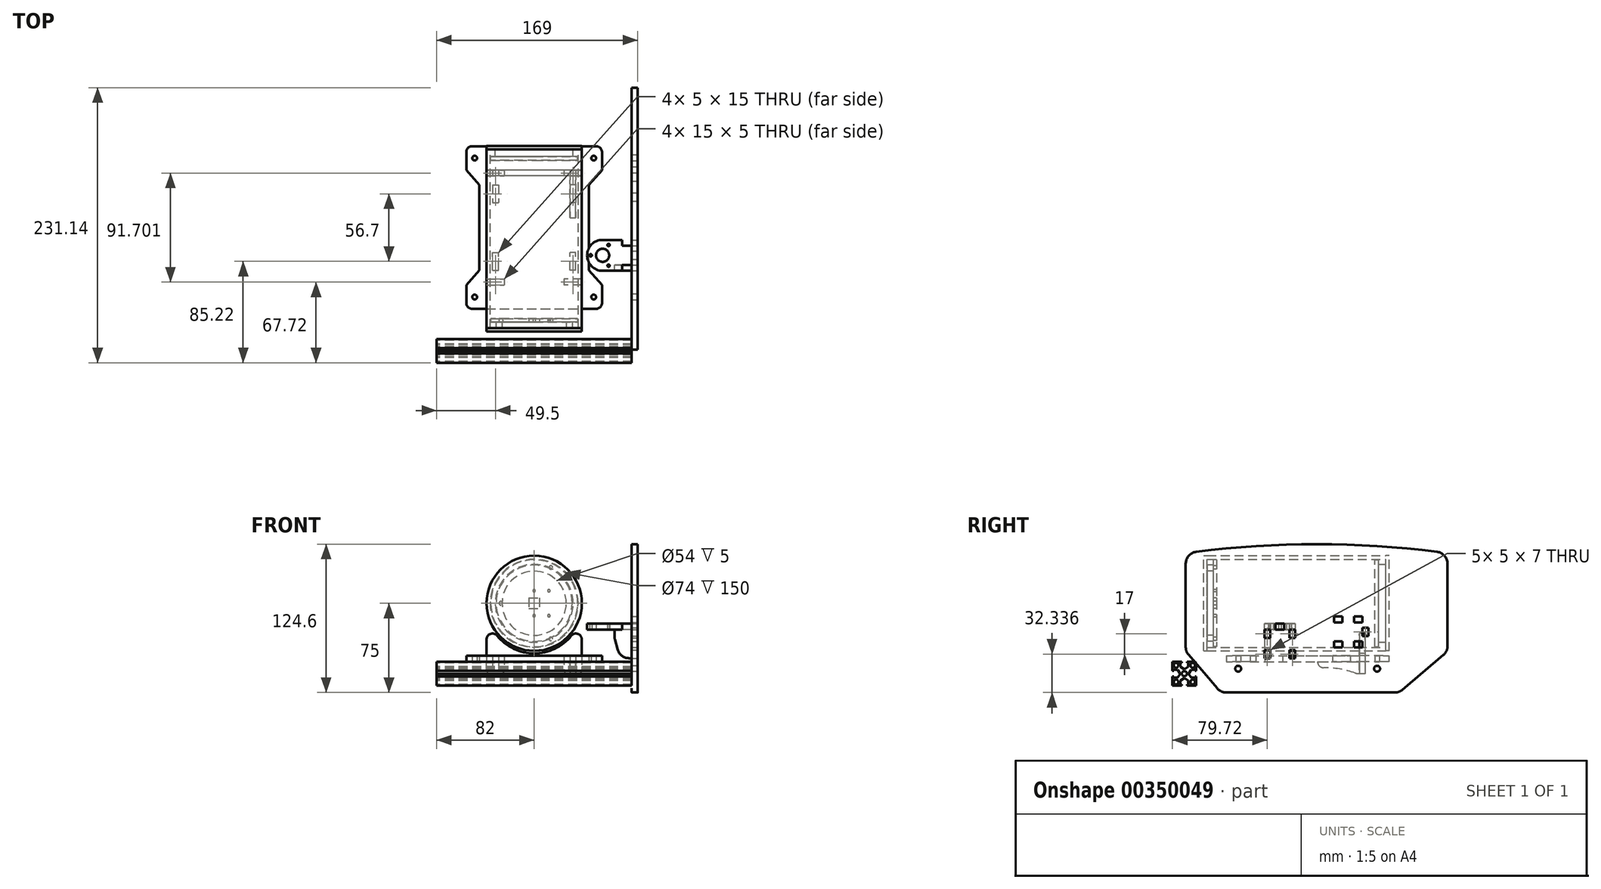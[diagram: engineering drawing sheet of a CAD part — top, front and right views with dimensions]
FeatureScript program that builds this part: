
annotation { "Feature Type Name" : "Feature", "Feature Type Description" : "" }
export const myFeature = defineFeature(function(context is Context, id is Id, definition is map)
    precondition{}
    {
        {
            var Q0;
            Q0=qCreatedBy(makeId("Front.planeOp"),FACE);
            var sketch = newSketch(context, id + "F0", { "sketchPlane" : qUnion([Q0])});
            skCircle(sketch, "E0", {"center": v(0, 0) * mm, "radius": 40 * mm});
            skCircle(sketch, "E1.0", {"center": v(0, 0) * mm, "radius": 37 * mm});
            skSolve(sketch);
        }
        {
            var Q0;
            Q0 = qSketchRegion(id + "F0", true);
            extrude(context, id + "F1", {"entities" : qUnion([Q0]), "depth" : 150 * mm});
        }
        {
            var Q0;
            Q0=makeQuery(id+"F1.opExtrude","CAP_FACE",FACE,{"disambiguationData":[OSD([sQuery(id+"F0.wireOp",EDGE,"E0"),sQuery(id+"F0.wireOp",EDGE,"E1.0")])],"isStart":false});
            var sketch = newSketch(context, id + "F2", { "sketchPlane" : qUnion([Q0])});
            skCircle(sketch, "E2", {"center": v(0, 0) * mm, "radius": 40 * mm});
            skSolve(sketch);
        }
        {
            var Q0;
            Q0=qSketchRegion(id+"F2",true);
            extrude(context, id + "F3", {"entities" : qUnion([Q0]), "depth" : 3 * mm});
        }
        {
            var Q0;
            Q0=makeQuery(id+"F3.opExtrude","CAP_FACE",FACE,{"disambiguationData":[OSD([sQuery(id+"F2.wireOp",EDGE,"E2")])],"isStart":true});
            var sketch = newSketch(context, id + "F4", { "sketchPlane" : qUnion([Q0])});
            skCircle(sketch, "E3", {"center": v(0, 0) * mm, "radius": 32 * mm});
            skCircle(sketch, "E4", {"center": v(0, 0) * mm, "radius": 27 * mm});
            skSolve(sketch);
        }
        {
            var Q0;
            Q0=qSketchRegion(id+"F4",true);
            extrude(context, id + "F5", {"entities" : qUnion([Q0]), "depth" : 5 * mm});
        }
        {
            var Q0;
            Q0=makeQuery(id+"F1.opExtrude","CAP_FACE",FACE,{"disambiguationData":[OSD([sQuery(id+"F0.wireOp",EDGE,"E0"),sQuery(id+"F0.wireOp",EDGE,"E1.0")])],"isStart":true});
            var sketch = newSketch(context, id + "F6", { "sketchPlane" : qUnion([Q0])});
            skCircle(sketch, "E5", {"center": v(0, 0) * mm, "radius": 40 * mm});
            skSolve(sketch);
        }
        {
            var Q0;
            Q0=qSketchRegion(id+"F6",true);
            extrude(context, id + "F7", {"entities" : qUnion([Q0]), "depth" : 3 * mm});
        }
        {
            var Q0;
            Q0=makeQuery(id+"F7.opExtrude","CAP_FACE",FACE,{"disambiguationData":[OSD([sQuery(id+"F6.wireOp",EDGE,"E5")])],"isStart":true});
            var sketch = newSketch(context, id + "F8", { "sketchPlane" : qUnion([Q0])});
            skCircle(sketch, "E6", {"center": v(0, 0) * mm, "radius": 37 * mm, "construction": true});
            skCircle(sketch, "E7", {"center": v(0, 0) * mm, "radius": 32.7 * mm});
            skSolve(sketch);
        }
        {
            var Q0;
            Q0=qSketchRegion(id+"F8",true);
            extrude(context, id + "F9", {"entities" : qUnion([Q0]), "depth" : 6 * mm});
        }
        {
            var Q0;
            Q0=makeQuery(id+"F9.opExtrude","CAP_FACE",FACE,{"disambiguationData":[OSD([sQuery(id+"F8.wireOp",EDGE,"E7")])],"isStart":false});
            var sketch = newSketch(context, id + "F10", { "sketchPlane" : qUnion([Q0])});
            skCircle(sketch, "E8", {"center": v(0, 0) * mm, "radius": 36.5 * mm});
            skSolve(sketch);
        }
        {
            var Q0;
            Q0=qSketchRegion(id+"F10",true);
            extrude(context, id + "F11", {"entities" : qUnion([Q0]), "depth" : 3 * mm});
        }
        {
            var Q0;
            Q0=makeQuery(id+"F5.opExtrude","CAP_FACE",FACE,{"disambiguationData":[OSD([sQuery(id+"F4.wireOp",EDGE,"E3"),sQuery(id+"F4.wireOp",EDGE,"E4")])],"isStart":false});
            var sketch = newSketch(context, id + "F12", { "sketchPlane" : qUnion([Q0])});
            skCircle(sketch, "E9", {"center": v(0, 0) * mm, "radius": 36.5 * mm});
            skCircle(sketch, "E10", {"center": v(28, 0) * mm, "radius": 1.5 * mm});
            skCircle(sketch, "E11", {"center": v(-14, 30) * mm, "radius": 1.5 * mm});
            skLineSegment(sketch, "E12", {"start": v(0, 0) * mm, "end": v(11.11, 0) * mm, "construction": true});
            skCircle(sketch, "E13.MirrorC", {"center": v(-14, -30) * mm, "radius": 1.5 * mm});
            skLineSegment(sketch, "E14.bottom", {"start": v(4.5, 4.5) * mm, "end": v(-4.5, 4.5) * mm});
            skLineSegment(sketch, "E14.top", {"start": v(4.5, -4.5) * mm, "end": v(-4.5, -4.5) * mm});
            skLineSegment(sketch, "E14.left", {"start": v(4.5, 4.5) * mm, "end": v(4.5, -4.5) * mm});
            skLineSegment(sketch, "E14.right", {"start": v(-4.5, 4.5) * mm, "end": v(-4.5, -4.5) * mm});
            skLineSegment(sketch, "E15.bottom", {"start": v(9.6, 12.5) * mm, "end": v(-14.4, 12.5) * mm, "construction": true});
            skLineSegment(sketch, "E15.top", {"start": v(9.6, -12.5) * mm, "end": v(-14.4, -12.5) * mm, "construction": true});
            skLineSegment(sketch, "E15.left", {"start": v(9.6, 12.5) * mm, "end": v(9.6, -12.5) * mm, "construction": true});
            skLineSegment(sketch, "E15.right", {"start": v(-14.4, 12.5) * mm, "end": v(-14.4, -12.5) * mm, "construction": true});
            skPoint(sketch, "E15.middle", {"position": v(-2.4, 0) * mm});
            skCircle(sketch, "E16", {"center": v(0.1, 10.5) * mm, "radius": 1.05 * mm});
            skCircle(sketch, "E17", {"center": v(-12.4, 10.5) * mm, "radius": 1.05 * mm});
            skCircle(sketch, "E18", {"center": v(-12.4, -10.5) * mm, "radius": 1.05 * mm});
            skCircle(sketch, "E19", {"center": v(0.1, -10.5) * mm, "radius": 1.05 * mm});
            skSolve(sketch);
        }
        {
            var Q0;
            Q0=qSketchRegion(id+"F12",true);
            extrude(context, id + "F13", {"entities" : qUnion([Q0]), "depth" : 3 * mm});
        }
        {
            var Q0;
            Q0=qCreatedBy(makeId("Right.planeOp"),FACE);
            var sketch = newSketch(context, id + "F14", { "sketchPlane" : qUnion([Q0])});
            skLineSegment(sketch, "E20.bottom", {"start": v(-159.14, -49.16) * mm, "end": v(-179.14, -49.16) * mm});
            skLineSegment(sketch, "E20.top", {"start": v(-159.14, -69.16) * mm, "end": v(-179.14, -69.16) * mm});
            skLineSegment(sketch, "E20.left", {"start": v(-159.14, -49.16) * mm, "end": v(-159.14, -69.16) * mm});
            skLineSegment(sketch, "E20.right", {"start": v(-179.14, -49.16) * mm, "end": v(-179.14, -69.16) * mm});
            skPoint(sketch, "E20.middle", {"position": v(-169.14, -59.16) * mm});
            skCircle(sketch, "E21", {"center": v(-169.14, -59.16) * mm, "radius": 2.15 * mm});
            skLineSegment(sketch, "E22", {"start": v(-169.14, -49.16) * mm, "end": v(-169.14, -69.16) * mm, "construction": true});
            skLineSegment(sketch, "E23", {"start": v(-179.14, -59.16) * mm, "end": v(-159.14, -59.16) * mm, "construction": true});
            skCircle(sketch, "E24", {"center": v(-176.14, -52.16) * mm, "radius": 2 * mm});
            skLineSegment(sketch, "E25", {"start": v(-169.14, -59.16) * mm, "end": v(-179.14, -49.16) * mm, "construction": true});
            skLineSegment(sketch, "E26", {"start": v(-171.44, -49.16) * mm, "end": v(-171.44, -50.16) * mm});
            skLineSegment(sketch, "E27", {"start": v(-171.44, -50.16) * mm, "end": v(-172.44, -50.16) * mm});
            skLineSegment(sketch, "E28", {"start": v(-172.44, -50.16) * mm, "end": v(-172.44, -53.36) * mm});
            skLineSegment(sketch, "E29", {"start": v(-172.44, -53.36) * mm, "end": v(-169.14, -55.66) * mm});
            skLineSegment(sketch, "E30.MirrorCS", {"start": v(-174.94, -55.86) * mm, "end": v(-172.64, -59.16) * mm});
            skLineSegment(sketch, "E31.MirrorCS", {"start": v(-178.14, -55.86) * mm, "end": v(-174.94, -55.86) * mm});
            skLineSegment(sketch, "E32.MirrorCS", {"start": v(-178.14, -56.86) * mm, "end": v(-178.14, -55.86) * mm});
            skLineSegment(sketch, "E33.MirrorCS", {"start": v(-179.14, -56.86) * mm, "end": v(-178.14, -56.86) * mm});
            skLineSegment(sketch, "E34.MirrorCS", {"start": v(-166.84, -49.16) * mm, "end": v(-166.84, -50.16) * mm});
            skLineSegment(sketch, "E35.MirrorCS", {"start": v(-166.84, -50.16) * mm, "end": v(-165.84, -50.16) * mm});
            skLineSegment(sketch, "E36.MirrorCS", {"start": v(-165.84, -50.16) * mm, "end": v(-165.84, -53.36) * mm});
            skLineSegment(sketch, "E37.MirrorCS", {"start": v(-165.84, -53.36) * mm, "end": v(-169.14, -55.66) * mm});
            skLineSegment(sketch, "E38.MirrorCS", {"start": v(-163.34, -55.86) * mm, "end": v(-165.64, -59.16) * mm});
            skLineSegment(sketch, "E39.MirrorCS", {"start": v(-160.14, -55.86) * mm, "end": v(-163.34, -55.86) * mm});
            skLineSegment(sketch, "E40.MirrorCS", {"start": v(-160.14, -56.86) * mm, "end": v(-160.14, -55.86) * mm});
            skLineSegment(sketch, "E41.MirrorCS", {"start": v(-159.14, -56.86) * mm, "end": v(-160.14, -56.86) * mm});
            skCircle(sketch, "E42.MirrorC", {"center": v(-162.14, -52.16) * mm, "radius": 2 * mm});
            skLineSegment(sketch, "E43.MirrorCS", {"start": v(-174.94, -62.46) * mm, "end": v(-172.64, -59.16) * mm});
            skLineSegment(sketch, "E44.MirrorCS", {"start": v(-178.14, -62.46) * mm, "end": v(-174.94, -62.46) * mm});
            skLineSegment(sketch, "E45.MirrorCS", {"start": v(-178.14, -61.46) * mm, "end": v(-178.14, -62.46) * mm});
            skLineSegment(sketch, "E46.MirrorCS", {"start": v(-179.14, -61.46) * mm, "end": v(-178.14, -61.46) * mm});
            skLineSegment(sketch, "E47.MirrorCS", {"start": v(-163.34, -62.46) * mm, "end": v(-165.64, -59.16) * mm});
            skLineSegment(sketch, "E48.MirrorCS", {"start": v(-160.14, -62.46) * mm, "end": v(-163.34, -62.46) * mm});
            skLineSegment(sketch, "E49.MirrorCS", {"start": v(-160.14, -61.46) * mm, "end": v(-160.14, -62.46) * mm});
            skLineSegment(sketch, "E50.MirrorCS", {"start": v(-159.14, -61.46) * mm, "end": v(-160.14, -61.46) * mm});
            skCircle(sketch, "E51.MirrorC", {"center": v(-162.14, -66.16) * mm, "radius": 2 * mm});
            skCircle(sketch, "E52.MirrorC", {"center": v(-176.14, -66.16) * mm, "radius": 2 * mm});
            skLineSegment(sketch, "E53.MirrorCS", {"start": v(-172.44, -64.96) * mm, "end": v(-169.14, -62.66) * mm});
            skLineSegment(sketch, "E54.MirrorCS", {"start": v(-172.44, -68.16) * mm, "end": v(-172.44, -64.96) * mm});
            skLineSegment(sketch, "E55.MirrorCS", {"start": v(-171.44, -68.16) * mm, "end": v(-172.44, -68.16) * mm});
            skLineSegment(sketch, "E56.MirrorCS", {"start": v(-171.44, -69.16) * mm, "end": v(-171.44, -68.16) * mm});
            skLineSegment(sketch, "E57.MirrorCS", {"start": v(-166.84, -69.16) * mm, "end": v(-166.84, -68.16) * mm});
            skLineSegment(sketch, "E58.MirrorCS", {"start": v(-166.84, -68.16) * mm, "end": v(-165.84, -68.16) * mm});
            skLineSegment(sketch, "E59.MirrorCS", {"start": v(-165.84, -68.16) * mm, "end": v(-165.84, -64.96) * mm});
            skLineSegment(sketch, "E60.MirrorCS", {"start": v(-165.84, -64.96) * mm, "end": v(-169.14, -62.66) * mm});
            skSolve(sketch);
        }
        {
            var Q0;
            Q0=makeQuery(id+"F14.imprint","IMPRINT",FACE,{"disambiguationData":[TD([[makeQuery(id+"F14.imprint","IMPRINT",EDGE,{"derivedFrom":sQuery(id+"F14.wireOp",EDGE,"E21")}),-1.0]])]});
            extrude(context, id + "F15", {"entities" : qUnion([Q0]), "depth" : 82 * mm, "hasSecondDirection" : true, "secondDirectionOppositeDirection" : true, "secondDirectionDepth" : 82 * mm});
        }
        {
            var Q0;
            Q0=makeQuery(id+"F15.opExtrude","CAP_FACE",FACE,{"disambiguationData":[OSD([sQuery(id+"F14.wireOp",EDGE,"E20.bottom"),sQuery(id+"F14.wireOp",EDGE,"E20.top"),sQuery(id+"F14.wireOp",EDGE,"E20.left"),sQuery(id+"F14.wireOp",EDGE,"E20.right"),sQuery(id+"F14.wireOp",EDGE,"E21"),sQuery(id+"F14.wireOp",EDGE,"E24"),sQuery(id+"F14.wireOp",EDGE,"E26"),sQuery(id+"F14.wireOp",EDGE,"E27"),sQuery(id+"F14.wireOp",EDGE,"E28"),sQuery(id+"F14.wireOp",EDGE,"E29"),sQuery(id+"F14.wireOp",EDGE,"E30.MirrorCS"),sQuery(id+"F14.wireOp",EDGE,"E31.MirrorCS"),sQuery(id+"F14.wireOp",EDGE,"E32.MirrorCS"),sQuery(id+"F14.wireOp",EDGE,"E33.MirrorCS"),sQuery(id+"F14.wireOp",EDGE,"E34.MirrorCS"),sQuery(id+"F14.wireOp",EDGE,"E35.MirrorCS"),sQuery(id+"F14.wireOp",EDGE,"E36.MirrorCS"),sQuery(id+"F14.wireOp",EDGE,"E37.MirrorCS"),sQuery(id+"F14.wireOp",EDGE,"E38.MirrorCS"),sQuery(id+"F14.wireOp",EDGE,"E39.MirrorCS"),sQuery(id+"F14.wireOp",EDGE,"E40.MirrorCS"),sQuery(id+"F14.wireOp",EDGE,"E41.MirrorCS"),sQuery(id+"F14.wireOp",EDGE,"E42.MirrorC"),sQuery(id+"F14.wireOp",EDGE,"E43.MirrorCS"),sQuery(id+"F14.wireOp",EDGE,"E44.MirrorCS"),sQuery(id+"F14.wireOp",EDGE,"E45.MirrorCS"),sQuery(id+"F14.wireOp",EDGE,"E46.MirrorCS"),sQuery(id+"F14.wireOp",EDGE,"E47.MirrorCS"),sQuery(id+"F14.wireOp",EDGE,"E48.MirrorCS"),sQuery(id+"F14.wireOp",EDGE,"E49.MirrorCS"),sQuery(id+"F14.wireOp",EDGE,"E50.MirrorCS"),sQuery(id+"F14.wireOp",EDGE,"E51.MirrorC"),sQuery(id+"F14.wireOp",EDGE,"E52.MirrorC"),sQuery(id+"F14.wireOp",EDGE,"E53.MirrorCS"),sQuery(id+"F14.wireOp",EDGE,"E54.MirrorCS"),sQuery(id+"F14.wireOp",EDGE,"E55.MirrorCS"),sQuery(id+"F14.wireOp",EDGE,"E56.MirrorCS"),sQuery(id+"F14.wireOp",EDGE,"E57.MirrorCS"),sQuery(id+"F14.wireOp",EDGE,"E58.MirrorCS"),sQuery(id+"F14.wireOp",EDGE,"E59.MirrorCS"),sQuery(id+"F14.wireOp",EDGE,"E60.MirrorCS")])],"isStart":false});
            var sketch = newSketch(context, id + "F16", { "sketchPlane" : qUnion([Q0])});
            skLineSegment(sketch, "E61", {"start": v(-141.53, -71.49) * mm, "end": v(-165.6, -43.24) * mm});
            skLineSegment(sketch, "E62", {"start": v(-168, -36.76) * mm, "end": v(-168, 33.24) * mm});
            skLineSegment(sketch, "E63", {"start": v(-133.92, -75) * mm, "end": v(7.78, -75) * mm});
            skLineSegment(sketch, "E64", {"start": v(14.27, -72.6) * mm, "end": v(48.49, -43.43) * mm});
            skLineSegment(sketch, "E65", {"start": v(52, -35.83) * mm, "end": v(52, 33.24) * mm});
            skArc(sketch, "E66", {"start": v(43.27, 43.16) * mm, "mid": v(-58, 49.6) * mm, "end": v(-159.27, 43.16) * mm});
            skPoint(sketch, "E67.visualSharp", {"position": v(-168, 42) * mm});
            skArc(sketch, "E67.filletArc", {"start": v(-159.27, 43.16) * mm, "mid": v(-165.5, 39.85) * mm, "end": v(-168, 33.24) * mm});
            skPoint(sketch, "E68.visualSharp", {"position": v(52, 42) * mm});
            skArc(sketch, "E68.filletArc", {"start": v(52, 33.24) * mm, "mid": v(49.5, 39.85) * mm, "end": v(43.27, 43.16) * mm});
            skPoint(sketch, "E69.visualSharp", {"position": v(-168, -40.44) * mm});
            skArc(sketch, "E69.filletArc", {"start": v(-168, -36.76) * mm, "mid": v(-167.38, -40.21) * mm, "end": v(-165.6, -43.24) * mm});
            skPoint(sketch, "E70.visualSharp", {"position": v(-138.53, -75) * mm});
            skArc(sketch, "E70.filletArc", {"start": v(-141.53, -71.49) * mm, "mid": v(-138.1, -74.08) * mm, "end": v(-133.92, -75) * mm});
            skPoint(sketch, "E71.visualSharp", {"position": v(11.47, -75) * mm});
            skArc(sketch, "E71.filletArc", {"start": v(7.78, -75) * mm, "mid": v(11.24, -74.38) * mm, "end": v(14.27, -72.6) * mm});
            skPoint(sketch, "E72.visualSharp", {"position": v(52, -40.44) * mm});
            skArc(sketch, "E72.filletArc", {"start": v(48.49, -43.43) * mm, "mid": v(51.08, -40.02) * mm, "end": v(52, -35.83) * mm});
            skCircle(sketch, "E73", {"center": v(-123.92, -55) * mm, "radius": 2.5 * mm});
            skCircle(sketch, "E74", {"center": v(-7.22, -55) * mm, "radius": 2.5 * mm});
            skSolve(sketch);
        }
        {
            var Q0;
            Q0=qSketchRegion(id+"F16",true);
            extrude(context, id + "F17", {"entities" : qUnion([Q0]), "depth" : 5 * mm});
        }
        {
            var Q0;
            {var subQ0=sQuery(id+"F14.wireOp",EDGE,"E20.bottom");Q0=makeQuery(id+"F15.opExtrude","SWEPT_FACE",FACE,{"disambiguationData":[OSD([subQ0]),TDD([makeQuery(id+"F14.imprint","IMPRINT",EDGE,{"disambiguationData":[TD([[makeQuery(id+"F14.imprint","INTERSECT",VERTEX,{"derivedFrom":[subQ0,sQuery(id+"F14.wireOp",EDGE,"E20.left")]}),-1.0]])],"derivedFrom":subQ0})])]});}
            var sketch = newSketch(context, id + "F18", { "sketchPlane" : qUnion([Q0])});
            skLineSegment(sketch, "E75.bottom", {"start": v(-82, 2.78) * mm, "end": v(82, 2.78) * mm});
            skLineSegment(sketch, "E75.top", {"start": v(-82, -133.92) * mm, "end": v(82, -133.92) * mm});
            skLineSegment(sketch, "E75.left", {"start": v(-82, 2.78) * mm, "end": v(-82, -133.92) * mm, "construction": true});
            skLineSegment(sketch, "E75.right", {"start": v(82, 2.78) * mm, "end": v(82, -133.92) * mm, "construction": true});
            skPoint(sketch, "E75.middle", {"position": v(0, -65.57) * mm});
            skLineSegment(sketch, "E76", {"start": v(-82, -113.92) * mm, "end": v(82, -113.92) * mm, "construction": true});
            skLineSegment(sketch, "E77", {"start": v(-82, -17.22) * mm, "end": v(82, -17.22) * mm, "construction": true});
            skLineSegment(sketch, "E78", {"start": v(0, -65.57) * mm, "end": v(0, -16.17) * mm, "construction": true});
            skLineSegment(sketch, "E79.bottom", {"start": v(40, -17.22) * mm, "end": v(25, -17.22) * mm});
            skLineSegment(sketch, "E79.top", {"start": v(40, -22.22) * mm, "end": v(25, -22.22) * mm});
            skLineSegment(sketch, "E79.left", {"start": v(40, -17.22) * mm, "end": v(40, -22.22) * mm});
            skLineSegment(sketch, "E79.right", {"start": v(25, -17.22) * mm, "end": v(25, -22.22) * mm});
            skLineSegment(sketch, "E80.bottom", {"start": v(40, -108.92) * mm, "end": v(25, -108.92) * mm});
            skLineSegment(sketch, "E80.top", {"start": v(40, -113.92) * mm, "end": v(25, -113.92) * mm});
            skLineSegment(sketch, "E80.left", {"start": v(40, -108.92) * mm, "end": v(40, -113.92) * mm});
            skLineSegment(sketch, "E80.right", {"start": v(25, -108.92) * mm, "end": v(25, -113.92) * mm});
            skLineSegment(sketch, "E81.MirrorCS", {"start": v(-25, -17.22) * mm, "end": v(-25, -22.22) * mm});
            skLineSegment(sketch, "E82.MirrorCS", {"start": v(-40, -17.22) * mm, "end": v(-25, -17.22) * mm});
            skLineSegment(sketch, "E83.MirrorCS", {"start": v(-40, -17.22) * mm, "end": v(-40, -22.22) * mm});
            skLineSegment(sketch, "E84.MirrorCS", {"start": v(-40, -22.22) * mm, "end": v(-25, -22.22) * mm});
            skLineSegment(sketch, "E85.MirrorCS", {"start": v(-40, -108.92) * mm, "end": v(-25, -108.92) * mm});
            skLineSegment(sketch, "E86.MirrorCS", {"start": v(-40, -108.92) * mm, "end": v(-40, -113.92) * mm});
            skLineSegment(sketch, "E87.MirrorCS", {"start": v(-40, -113.92) * mm, "end": v(-25, -113.92) * mm});
            skLineSegment(sketch, "E88.MirrorCS", {"start": v(-25, -108.92) * mm, "end": v(-25, -113.92) * mm});
            skLineSegment(sketch, "E89", {"start": v(-57, 2.78) * mm, "end": v(-57, -133.92) * mm});
            skLineSegment(sketch, "E90", {"start": v(57, 2.78) * mm, "end": v(57, -133.92) * mm});
            skLineSegment(sketch, "E91.bottom", {"start": v(35, -29.72) * mm, "end": v(30, -29.72) * mm});
            skLineSegment(sketch, "E91.top", {"start": v(35, -44.72) * mm, "end": v(30, -44.72) * mm});
            skLineSegment(sketch, "E91.left", {"start": v(35, -29.72) * mm, "end": v(35, -44.72) * mm});
            skLineSegment(sketch, "E91.right", {"start": v(30, -29.72) * mm, "end": v(30, -44.72) * mm});
            skPoint(sketch, "E91.middle", {"position": v(32.5, -37.22) * mm});
            skPoint(sketch, "E92", {"position": v(32.5, -22.22) * mm});
            skLineSegment(sketch, "E93", {"start": v(0, -65.57) * mm, "end": v(25.4, -65.57) * mm, "construction": true});
            skLineSegment(sketch, "E94.MirrorCS", {"start": v(35, -86.42) * mm, "end": v(30, -86.42) * mm});
            skLineSegment(sketch, "E95.MirrorCS", {"start": v(35, -101.42) * mm, "end": v(35, -86.42) * mm});
            skLineSegment(sketch, "E96.MirrorCS", {"start": v(35, -101.42) * mm, "end": v(30, -101.42) * mm});
            skLineSegment(sketch, "E97.MirrorCS", {"start": v(30, -101.42) * mm, "end": v(30, -86.42) * mm});
            skLineSegment(sketch, "E98.MirrorCS", {"start": v(-30, -29.72) * mm, "end": v(-30, -44.72) * mm});
            skLineSegment(sketch, "E99.MirrorCS", {"start": v(-35, -29.72) * mm, "end": v(-30, -29.72) * mm});
            skLineSegment(sketch, "E100.MirrorCS", {"start": v(-35, -29.72) * mm, "end": v(-35, -44.72) * mm});
            skLineSegment(sketch, "E101.MirrorCS", {"start": v(-35, -44.72) * mm, "end": v(-30, -44.72) * mm});
            skLineSegment(sketch, "E102.MirrorCS", {"start": v(-35, -86.42) * mm, "end": v(-30, -86.42) * mm});
            skLineSegment(sketch, "E103.MirrorCS", {"start": v(-30, -101.42) * mm, "end": v(-30, -86.42) * mm});
            skLineSegment(sketch, "E104.MirrorCS", {"start": v(-35, -101.42) * mm, "end": v(-35, -86.42) * mm});
            skLineSegment(sketch, "E105.MirrorCS", {"start": v(-35, -101.42) * mm, "end": v(-30, -101.42) * mm});
            skLineSegment(sketch, "E106.0", {"start": v(87, -121.42) * mm, "end": v(87, -126.42) * mm, "construction": true});
            skLineSegment(sketch, "E107.0", {"start": v(87, -4.72) * mm, "end": v(87, -9.72) * mm, "construction": true});
            skPoint(sketch, "E108", {"position": v(87, -123.92) * mm});
            skPoint(sketch, "E109", {"position": v(87, -7.22) * mm});
            skLineSegment(sketch, "E110", {"start": v(-57, -113.92) * mm, "end": v(-46, -101.57) * mm});
            skLineSegment(sketch, "E111", {"start": v(-46, -101.57) * mm, "end": v(-46, -29.57) * mm});
            skLineSegment(sketch, "E112", {"start": v(-46, -29.57) * mm, "end": v(-57, -17.22) * mm});
            skPoint(sketch, "E113", {"position": v(-57, -65.57) * mm});
            skPoint(sketch, "E114", {"position": v(-46, -65.57) * mm});
            skLineSegment(sketch, "E115.MirrorCS", {"start": v(57, -113.92) * mm, "end": v(46, -101.57) * mm});
            skLineSegment(sketch, "E116.MirrorCS", {"start": v(46, -101.57) * mm, "end": v(46, -29.57) * mm});
            skLineSegment(sketch, "E117.MirrorCS", {"start": v(46, -29.57) * mm, "end": v(57, -17.22) * mm});
            skCircle(sketch, "E118", {"center": v(50, -123.92) * mm, "radius": 2 * mm});
            skCircle(sketch, "E119.MirrorC", {"center": v(-50, -123.92) * mm, "radius": 2 * mm});
            skCircle(sketch, "E120.MirrorC", {"center": v(50, -7.22) * mm, "radius": 2 * mm});
            skCircle(sketch, "E121.MirrorC", {"center": v(-50, -7.22) * mm, "radius": 2 * mm});
            skSolve(sketch);
        }
        {
            var Q0;
            {var subQ5=sQuery(id+"F18.wireOp",EDGE,"E75.bottom");Q0=makeQuery(id+"F18.imprint","IMPRINT",FACE,{"disambiguationData":[TD([[makeQuery(id+"F18.imprint","IMPRINT",EDGE,{"derivedFrom":subQ5}),-1.0]])]});}
            extrude(context, id + "F19", {"entities" : qUnion([Q0]), "depth" : 5 * mm});
        }
        {
            var Q0;
            Q0=makeQuery(id+"F19.opExtrude","SWEPT_FACE",FACE,{"disambiguationData":[OSD([sQuery(id+"F18.wireOp",EDGE,"E79.top")])]});
            var sketch = newSketch(context, id + "F20", { "sketchPlane" : qUnion([Q0])});
            skLineSegment(sketch, "E122", {"start": v(-40, -30.45) * mm, "end": v(-40, -56.16) * mm});
            skLineSegment(sketch, "E123", {"start": v(-37, -59.16) * mm, "end": v(-28, -59.16) * mm});
            skLineSegment(sketch, "E124", {"start": v(-25, -56.16) * mm, "end": v(-25, -44.16) * mm});
            skLineSegment(sketch, "E125", {"start": v(-25, -44.16) * mm, "end": v(25, -44.16) * mm});
            skLineSegment(sketch, "E126", {"start": v(25, -44.16) * mm, "end": v(25, -56.16) * mm});
            skLineSegment(sketch, "E127", {"start": v(28, -59.16) * mm, "end": v(37, -59.16) * mm});
            skLineSegment(sketch, "E128", {"start": v(40, -56.16) * mm, "end": v(40, -30.45) * mm});
            skArc(sketch, "E129", {"start": v(-31.11, -27.3) * mm, "mid": v(0, -42.16) * mm, "end": v(31.11, -27.3) * mm});
            skPoint(sketch, "E130.visualSharp", {"position": v(-40, -2.16) * mm});
            skArc(sketch, "E130.filletArc", {"start": v(-31.11, -27.3) * mm, "mid": v(-36.67, -25.73) * mm, "end": v(-40, -30.45) * mm});
            skPoint(sketch, "E131.visualSharp", {"position": v(40, -2.16) * mm});
            skArc(sketch, "E131.filletArc", {"start": v(40, -30.45) * mm, "mid": v(36.67, -25.73) * mm, "end": v(31.11, -27.3) * mm});
            skPoint(sketch, "E132.visualSharp", {"position": v(-40, -59.16) * mm});
            skArc(sketch, "E132.filletArc", {"start": v(-40, -56.16) * mm, "mid": v(-39.12, -58.29) * mm, "end": v(-37, -59.16) * mm});
            skPoint(sketch, "E133.visualSharp", {"position": v(-25, -59.16) * mm});
            skArc(sketch, "E133.filletArc", {"start": v(-28, -59.16) * mm, "mid": v(-25.88, -58.29) * mm, "end": v(-25, -56.16) * mm});
            skPoint(sketch, "E134.visualSharp", {"position": v(25, -59.16) * mm});
            skArc(sketch, "E134.filletArc", {"start": v(25, -56.16) * mm, "mid": v(25.88, -58.29) * mm, "end": v(28, -59.16) * mm});
            skPoint(sketch, "E135.visualSharp", {"position": v(40, -59.16) * mm});
            skArc(sketch, "E135.filletArc", {"start": v(37, -59.16) * mm, "mid": v(39.12, -58.29) * mm, "end": v(40, -56.16) * mm});
            skLineSegment(sketch, "E136.bottom", {"start": v(-35, -49.16) * mm, "end": v(-30, -49.16) * mm});
            skLineSegment(sketch, "E136.top", {"start": v(-35, -69.16) * mm, "end": v(-30, -69.16) * mm});
            skLineSegment(sketch, "E136.left", {"start": v(-35, -49.16) * mm, "end": v(-35, -69.16) * mm});
            skLineSegment(sketch, "E136.right", {"start": v(-30, -49.16) * mm, "end": v(-30, -69.16) * mm});
            skPoint(sketch, "E136.middle", {"position": v(-32.5, -59.16) * mm});
            skLineSegment(sketch, "E137.bottom", {"start": v(30, -49.16) * mm, "end": v(35, -49.16) * mm});
            skLineSegment(sketch, "E137.top", {"start": v(30, -69.16) * mm, "end": v(35, -69.16) * mm});
            skLineSegment(sketch, "E137.left", {"start": v(30, -49.16) * mm, "end": v(30, -69.16) * mm});
            skLineSegment(sketch, "E137.right", {"start": v(35, -49.16) * mm, "end": v(35, -69.16) * mm});
            skPoint(sketch, "E137.middle", {"position": v(32.5, -59.16) * mm});
            skSolve(sketch);
        }
        {
            var Q0;
            Q0=makeQuery(id+"F20.imprint","IMPRINT",FACE,{"disambiguationData":[TD([[makeQuery(id+"F20.imprint","IMPRINT",EDGE,{"derivedFrom":sQuery(id+"F20.wireOp",EDGE,"E125")}),1.0]])]});
            var Q1;
            {var subQ5=sQuery(id+"F20.wireOp",EDGE,"E136.bottom");Q1=makeQuery(id+"F20.imprint","IMPRINT",FACE,{"disambiguationData":[TD([[makeQuery(id+"F20.imprint","IMPRINT",EDGE,{"derivedFrom":subQ5}),1.0]])]});}
            var Q2;
            {var subQ7=sQuery(id+"F20.wireOp",EDGE,"E132.filletArc");Q2=makeQuery(id+"F20.imprint","IMPRINT",FACE,{"disambiguationData":[TD([[makeQuery(id+"F20.imprint","IMPRINT",EDGE,{"derivedFrom":subQ7}),1.0]])]});}
            var Q3;
            {var subQ0=sQuery(id+"F20.wireOp",EDGE,"E133.filletArc");Q3=makeQuery(id+"F20.imprint","IMPRINT",FACE,{"disambiguationData":[TD([[makeQuery(id+"F20.imprint","IMPRINT",EDGE,{"derivedFrom":subQ0}),1.0]])]});}
            extrude(context, id + "F21", {"entities" : qUnion([Q0, Q1, Q2, Q3]), "depth" : 5 * mm});
        }
        {
            var Q0;
            Q0=makeQuery(id+"F19.opExtrude","SWEPT_EDGE",EDGE,{"disambiguationData":[OSD([sQuery(id+"F18.wireOp",EDGE,"E75.bottom"),sQuery(id+"F18.wireOp",EDGE,"E89")])]});
            var Q1;
            Q1=makeQuery(id+"F19.opExtrude","SWEPT_EDGE",EDGE,{"disambiguationData":[OSD([sQuery(id+"F18.wireOp",EDGE,"E75.bottom"),sQuery(id+"F18.wireOp",EDGE,"E90")])]});
            var Q2;
            Q2=makeQuery(id+"F19.opExtrude","SWEPT_EDGE",EDGE,{"disambiguationData":[OSD([sQuery(id+"F18.wireOp",EDGE,"E75.top"),sQuery(id+"F18.wireOp",EDGE,"E89")])]});
            var Q3;
            Q3=makeQuery(id+"F19.opExtrude","SWEPT_EDGE",EDGE,{"disambiguationData":[OSD([sQuery(id+"F18.wireOp",EDGE,"E75.top"),sQuery(id+"F18.wireOp",EDGE,"E90")])]});
            fillet(context, id + "F22", {"entities" : qUnion([Q0, Q1, Q2, Q3]), "radius" : 5 * mm, "tangentPropagation" : true, "allowEdgeOverflow" : false});
        }
        {
            var Q0;
            Q0=makeQuery(id+"F21.opExtrude","SWEPT_FACE",FACE,{"disambiguationData":[OSD([sQuery(id+"F20.wireOp",EDGE,"E136.left")])]});
            var sketch = newSketch(context, id + "F23", { "sketchPlane" : qUnion([Q0])});
            skLineSegment(sketch, "E138", {"start": v(17.22, -49.16) * mm, "end": v(17.22, -59.16) * mm});
            skLineSegment(sketch, "E139", {"start": v(17.22, -59.16) * mm, "end": v(22.22, -59.16) * mm});
            skPoint(sketch, "E139.endSnap0", {"position": v(19.72, -59.16) * mm});
            skLineSegment(sketch, "E140", {"start": v(57.22, -49.16) * mm, "end": v(17.22, -49.16) * mm});
            skArc(sketch, "E141", {"start": v(52.22, -54.16) * mm, "mid": v(38.66, -55.29) * mm, "end": v(25.46, -58.62) * mm});
            skPoint(sketch, "E142.visualSharp", {"position": v(23.93, -59.16) * mm});
            skArc(sketch, "E142.filletArc", {"start": v(22.22, -59.16) * mm, "mid": v(23.86, -59.03) * mm, "end": v(25.46, -58.62) * mm});
            skArc(sketch, "E143", {"start": v(52.22, -54.16) * mm, "mid": v(55.75, -52.7) * mm, "end": v(57.22, -49.16) * mm});
            skLineSegment(sketch, "E144", {"start": v(42.42, -54.16) * mm, "end": v(52.22, -54.16) * mm, "construction": true});
            skLineSegment(sketch, "E145.bottom", {"start": v(29.72, -44.16) * mm, "end": v(44.72, -44.16) * mm});
            skLineSegment(sketch, "E145.top", {"start": v(29.72, -49.16) * mm, "end": v(44.72, -49.16) * mm});
            skLineSegment(sketch, "E145.left", {"start": v(29.72, -44.16) * mm, "end": v(29.72, -49.16) * mm});
            skLineSegment(sketch, "E145.right", {"start": v(44.72, -44.16) * mm, "end": v(44.72, -49.16) * mm});
            skSolve(sketch);
        }
        {
            var Q0;
            Q0=qSketchRegion(id+"F23",true);
            extrude(context, id + "F24", {"entities" : qUnion([Q0]), "depth" : 5 * mm});
        }
        {
            var Q0;
            Q0=makeQuery(id+"F17.opExtrude","CAP_FACE",FACE,{"disambiguationData":[OSD([sQuery(id+"F16.wireOp",EDGE,"E61"),sQuery(id+"F16.wireOp",EDGE,"E62"),sQuery(id+"F16.wireOp",EDGE,"E63"),sQuery(id+"F16.wireOp",EDGE,"E64"),sQuery(id+"F16.wireOp",EDGE,"E65"),sQuery(id+"F16.wireOp",EDGE,"E66"),sQuery(id+"F16.wireOp",EDGE,"E67.filletArc"),sQuery(id+"F16.wireOp",EDGE,"E68.filletArc"),sQuery(id+"F16.wireOp",EDGE,"E69.filletArc"),sQuery(id+"F16.wireOp",EDGE,"E70.filletArc"),sQuery(id+"F16.wireOp",EDGE,"E71.filletArc"),sQuery(id+"F16.wireOp",EDGE,"E72.filletArc"),sQuery(id+"F16.wireOp",EDGE,"E73"),sQuery(id+"F16.wireOp",EDGE,"E74")])],"isStart":false});
            var sketch = newSketch(context, id + "F25", { "sketchPlane" : qUnion([Q0])});
            skLineSegment(sketch, "E146.bottom", {"start": v(-101.92, -22.16) * mm, "end": v(-96.92, -22.16) * mm});
            skLineSegment(sketch, "E146.top", {"start": v(-101.92, -29.16) * mm, "end": v(-96.92, -29.16) * mm});
            skLineSegment(sketch, "E146.left", {"start": v(-101.92, -22.16) * mm, "end": v(-101.92, -29.16) * mm});
            skLineSegment(sketch, "E146.right", {"start": v(-96.92, -22.16) * mm, "end": v(-96.92, -29.16) * mm});
            skLineSegment(sketch, "E147.bottom", {"start": v(-101.92, -39.16) * mm, "end": v(-96.92, -39.16) * mm});
            skLineSegment(sketch, "E147.top", {"start": v(-101.92, -46.16) * mm, "end": v(-96.92, -46.16) * mm});
            skLineSegment(sketch, "E147.left", {"start": v(-101.92, -39.16) * mm, "end": v(-101.92, -46.16) * mm});
            skLineSegment(sketch, "E147.right", {"start": v(-96.92, -39.16) * mm, "end": v(-96.92, -46.16) * mm});
            skLineSegment(sketch, "E148", {"start": v(-88.92, 8.82) * mm, "end": v(-88.92, -36.9) * mm, "construction": true});
            skLineSegment(sketch, "E149.MirrorCS", {"start": v(-75.92, -39.16) * mm, "end": v(-80.92, -39.16) * mm});
            skLineSegment(sketch, "E150.MirrorCS", {"start": v(-80.92, -22.16) * mm, "end": v(-80.92, -29.16) * mm});
            skLineSegment(sketch, "E151.MirrorCS", {"start": v(-75.92, -22.16) * mm, "end": v(-75.92, -29.16) * mm});
            skLineSegment(sketch, "E152.MirrorCS", {"start": v(-80.92, -39.16) * mm, "end": v(-80.92, -46.16) * mm});
            skLineSegment(sketch, "E153.MirrorCS", {"start": v(-75.92, -46.16) * mm, "end": v(-80.92, -46.16) * mm});
            skLineSegment(sketch, "E154.MirrorCS", {"start": v(-75.92, -39.16) * mm, "end": v(-75.92, -46.16) * mm});
            skLineSegment(sketch, "E155.MirrorCS", {"start": v(-75.92, -22.16) * mm, "end": v(-80.92, -22.16) * mm});
            skLineSegment(sketch, "E156.MirrorCS", {"start": v(-75.92, -29.16) * mm, "end": v(-80.92, -29.16) * mm});
            skLineSegment(sketch, "E157.bottom", {"start": v(-92.42, -17.16) * mm, "end": v(-85.42, -17.16) * mm});
            skLineSegment(sketch, "E157.top", {"start": v(-92.42, -22.16) * mm, "end": v(-85.42, -22.16) * mm});
            skLineSegment(sketch, "E157.left", {"start": v(-92.42, -17.16) * mm, "end": v(-92.42, -22.16) * mm});
            skLineSegment(sketch, "E157.right", {"start": v(-85.42, -17.16) * mm, "end": v(-85.42, -22.16) * mm});
            skPoint(sketch, "E157.middle", {"position": v(-88.92, -19.66) * mm});
            skLineSegment(sketch, "E158", {"start": v(-61.44, -24.16) * mm, "end": v(0.92, -24.16) * mm, "construction": true});
            skLineSegment(sketch, "E159.bottom", {"start": v(-14.5, -20.66) * mm, "end": v(-19.5, -20.66) * mm});
            skLineSegment(sketch, "E159.top", {"start": v(-14.5, -27.66) * mm, "end": v(-19.5, -27.66) * mm});
            skLineSegment(sketch, "E159.left", {"start": v(-14.5, -20.66) * mm, "end": v(-14.5, -27.66) * mm});
            skLineSegment(sketch, "E159.right", {"start": v(-19.5, -20.66) * mm, "end": v(-19.5, -27.66) * mm});
            skPoint(sketch, "E159.middle", {"position": v(-17, -24.16) * mm});
            skLineSegment(sketch, "E160.bottom", {"start": v(-26.5, -11.16) * mm, "end": v(-19.5, -11.16) * mm});
            skLineSegment(sketch, "E160.top", {"start": v(-26.5, -16.16) * mm, "end": v(-19.5, -16.16) * mm});
            skLineSegment(sketch, "E160.left", {"start": v(-26.5, -11.16) * mm, "end": v(-26.5, -16.16) * mm});
            skLineSegment(sketch, "E160.right", {"start": v(-19.5, -11.16) * mm, "end": v(-19.5, -16.16) * mm});
            skPoint(sketch, "E160.middle", {"position": v(-23, -13.66) * mm});
            skLineSegment(sketch, "E161.bottom", {"start": v(-43.5, -11.16) * mm, "end": v(-36.5, -11.16) * mm});
            skLineSegment(sketch, "E161.top", {"start": v(-43.5, -16.16) * mm, "end": v(-36.5, -16.16) * mm});
            skLineSegment(sketch, "E161.left", {"start": v(-43.5, -11.16) * mm, "end": v(-43.5, -16.16) * mm});
            skLineSegment(sketch, "E161.right", {"start": v(-36.5, -11.16) * mm, "end": v(-36.5, -16.16) * mm});
            skPoint(sketch, "E161.middle", {"position": v(-40, -13.66) * mm});
            skLineSegment(sketch, "E162.MirrorCS", {"start": v(-26.5, -32.16) * mm, "end": v(-19.5, -32.16) * mm});
            skLineSegment(sketch, "E163.MirrorCS", {"start": v(-43.5, -32.16) * mm, "end": v(-36.5, -32.16) * mm});
            skLineSegment(sketch, "E164.MirrorCS", {"start": v(-43.5, -37.16) * mm, "end": v(-36.5, -37.16) * mm});
            skLineSegment(sketch, "E165.MirrorCS", {"start": v(-36.5, -37.16) * mm, "end": v(-36.5, -32.16) * mm});
            skLineSegment(sketch, "E166.MirrorCS", {"start": v(-19.5, -37.16) * mm, "end": v(-19.5, -32.16) * mm});
            skLineSegment(sketch, "E167.MirrorCS", {"start": v(-26.5, -37.16) * mm, "end": v(-26.5, -32.16) * mm});
            skLineSegment(sketch, "E168.MirrorCS", {"start": v(-43.5, -37.16) * mm, "end": v(-43.5, -32.16) * mm});
            skPoint(sketch, "E169.MirrorP", {"position": v(-23, -34.66) * mm});
            skPoint(sketch, "E170.MirrorP", {"position": v(-40, -34.66) * mm});
            skLineSegment(sketch, "E171.MirrorCS", {"start": v(-26.5, -37.16) * mm, "end": v(-19.5, -37.16) * mm});
            skSolve(sketch);
        }
        {
            var Q0;
            Q0=makeQuery(id+"F25.imprint","IMPRINT",FACE,{"disambiguationData":[TD([[makeQuery(id+"F25.imprint","IMPRINT",EDGE,{"derivedFrom":sQuery(id+"F25.wireOp",EDGE,"E146.bottom")}),-1.0]])]});
            var Q1;
            Q1=makeQuery(id+"F25.imprint","IMPRINT",FACE,{"disambiguationData":[TD([[makeQuery(id+"F25.imprint","IMPRINT",EDGE,{"derivedFrom":sQuery(id+"F25.wireOp",EDGE,"E147.bottom")}),-1.0]])]});
            var Q2;
            Q2=makeQuery(id+"F25.imprint","IMPRINT",FACE,{"disambiguationData":[TD([[makeQuery(id+"F25.imprint","IMPRINT",EDGE,{"derivedFrom":sQuery(id+"F25.wireOp",EDGE,"E149.MirrorCS")}),1.0]])]});
            var Q3;
            Q3=makeQuery(id+"F25.imprint","IMPRINT",FACE,{"disambiguationData":[TD([[makeQuery(id+"F25.imprint","IMPRINT",EDGE,{"derivedFrom":sQuery(id+"F25.wireOp",EDGE,"E150.MirrorCS")}),1.0]])]});
            var Q4;
            Q4=makeQuery(id+"F25.imprint","IMPRINT",FACE,{"disambiguationData":[TD([[makeQuery(id+"F25.imprint","IMPRINT",EDGE,{"derivedFrom":sQuery(id+"F25.wireOp",EDGE,"E157.bottom")}),-1.0]])]});
            var Q5;
            Q5=makeQuery(id+"F25.imprint","IMPRINT",FACE,{"disambiguationData":[TD([[makeQuery(id+"F25.imprint","IMPRINT",EDGE,{"derivedFrom":sQuery(id+"F25.wireOp",EDGE,"E159.bottom")}),1.0]])]});
            var Q6;
            Q6=makeQuery(id+"F25.imprint","IMPRINT",FACE,{"disambiguationData":[TD([[makeQuery(id+"F25.imprint","IMPRINT",EDGE,{"derivedFrom":sQuery(id+"F25.wireOp",EDGE,"E160.bottom")}),-1.0]])]});
            var Q7;
            Q7=makeQuery(id+"F25.imprint","IMPRINT",FACE,{"disambiguationData":[TD([[makeQuery(id+"F25.imprint","IMPRINT",EDGE,{"derivedFrom":sQuery(id+"F25.wireOp",EDGE,"E161.bottom")}),-1.0]])]});
            var Q8;
            Q8=makeQuery(id+"F25.imprint","IMPRINT",FACE,{"disambiguationData":[TD([[makeQuery(id+"F25.imprint","IMPRINT",EDGE,{"derivedFrom":sQuery(id+"F25.wireOp",EDGE,"E162.MirrorCS")}),-1.0]])]});
            var Q9;
            Q9=makeQuery(id+"F25.imprint","IMPRINT",FACE,{"disambiguationData":[TD([[makeQuery(id+"F25.imprint","IMPRINT",EDGE,{"derivedFrom":sQuery(id+"F25.wireOp",EDGE,"E163.MirrorCS")}),-1.0]])]});
            var Q10;
            Q10=makeQuery(id+"F25.imprint","IMPRINT",FACE,{"disambiguationData":[TD([[makeQuery(id+"F25.imprint","IMPRINT",EDGE,{"derivedFrom":sQuery(id+"F25.wireOp",EDGE,"apbcTbPJ-BgK0-jB3Y-WGwL-rk3hIpp7gB95")}),-1.0]])]});
            var Q11;
            Q11=makeQuery(id+"F25.imprint","IMPRINT",FACE,{"disambiguationData":[TD([[makeQuery(id+"F25.imprint","IMPRINT",EDGE,{"derivedFrom":sQuery(id+"F25.wireOp",EDGE,"XGmMSYxH-nwvD-xv23-DNzk-bPtLV3bHt7pH")}),1.0]])]});
            var Q12;
            {var subQ0=sQuery(id+"F25.wireOp",EDGE,"BIz49tEz-hAjj-NARr-SRFq-i8sWeO4FZqb0");Q12=makeQuery(id+"F25.imprint","IMPRINT",FACE,{"disambiguationData":[TD([[makeQuery(id+"F25.imprint","IMPRINT",EDGE,{"derivedFrom":subQ0}),1.0]])]});}
            extrude(context, id + "F26", {"entities" : qUnion([Q0, Q1, Q2, Q3, Q4, Q5, Q6, Q7, Q8, Q9, Q10, Q11, Q12]), "operationType" : NewBodyOperationType.REMOVE, "oppositeDirection" : true, "depth" : 25 * mm});
        }
        {
            var Q0;
            Q0=makeQuery(id+"F26.boolean.opBoolean","COPY",FACE,{"derivedFrom":makeQuery(id+"F26.opExtrude","SWEPT_FACE",FACE,{"disambiguationData":[OSD([sQuery(id+"F25.wireOp",EDGE,"E157.top")])]})});
            var sketch = newSketch(context, id + "F27", { "sketchPlane" : qUnion([Q0])});
            skLineSegment(sketch, "E172.0.0", {"start": v(82, -92.42) * mm, "end": v(82, -85.42) * mm});
            skLineSegment(sketch, "E172.0.1", {"start": v(82, -85.42) * mm, "end": v(87, -85.42) * mm});
            skLineSegment(sketch, "E172.0.2", {"start": v(87, -85.42) * mm, "end": v(87, -92.42) * mm});
            skLineSegment(sketch, "E172.0.3", {"start": v(87, -92.42) * mm, "end": v(82, -92.42) * mm});
            skLineSegment(sketch, "E173", {"start": v(82, -85.42) * mm, "end": v(82, -80.92) * mm});
            skLineSegment(sketch, "E174", {"start": v(82, -80.92) * mm, "end": v(74, -80.92) * mm});
            skLineSegment(sketch, "E175", {"start": v(74, -80.92) * mm, "end": v(74, -75.92) * mm});
            skLineSegment(sketch, "E176", {"start": v(74, -75.92) * mm, "end": v(57.5, -75.92) * mm});
            skLineSegment(sketch, "E177", {"start": v(82, -92.42) * mm, "end": v(82, -96.92) * mm});
            skLineSegment(sketch, "E178", {"start": v(82, -96.92) * mm, "end": v(74, -96.92) * mm});
            skLineSegment(sketch, "E179", {"start": v(74, -96.92) * mm, "end": v(74, -101.92) * mm});
            skLineSegment(sketch, "E180", {"start": v(74, -101.92) * mm, "end": v(57.5, -101.92) * mm});
            skCircle(sketch, "E181", {"center": v(57.5, -88.92) * mm, "radius": 13 * mm});
            skCircle(sketch, "E182", {"center": v(57.5, -88.92) * mm, "radius": 22.5 * mm, "construction": true});
            skCircle(sketch, "E183", {"center": v(57.5, -88.92) * mm, "radius": 12.5 * mm, "construction": true});
            skCircle(sketch, "E184", {"center": v(47.5, -88.92) * mm, "radius": 1 * mm});
            skCircle(sketch, "E185.1.0", {"center": v(62.5, -97.58) * mm, "radius": 1 * mm});
            skCircle(sketch, "E185.2.0", {"center": v(62.5, -80.26) * mm, "radius": 1 * mm});
            skCircle(sketch, "E186", {"center": v(57.5, -88.92) * mm, "radius": 5.5 * mm});
            skSolve(sketch);
        }
        {
            var Q0;
            Q0=makeQuery(id+"F27.imprint","IMPRINT",FACE,{"disambiguationData":[TD([[makeQuery(id+"F27.imprint","IMPRINT",EDGE,{"derivedFrom":sQuery(id+"F27.wireOp",EDGE,"E172.0.0")}),1.0]])]});
            var Q1;
            Q1=makeQuery(id+"F27.imprint","IMPRINT",FACE,{"disambiguationData":[TD([[makeQuery(id+"F27.imprint","IMPRINT",EDGE,{"derivedFrom":sQuery(id+"F27.wireOp",EDGE,"E184")}),-1.0]])]});
            var Q2;
            Q2=makeQuery(id+"F27.imprint","IMPRINT",FACE,{"disambiguationData":[TD([[makeQuery(id+"F27.imprint","IMPRINT",EDGE,{"derivedFrom":sQuery(id+"F27.wireOp",EDGE,"E172.0.0")}),-1.0]])]});
            extrude(context, id + "F28", {"entities" : qUnion([Q0, Q1, Q2]), "depth" : 5 * mm});
        }
        {
            var Q0;
            Q0=makeQuery(id+"F26.boolean.opBoolean","COPY",FACE,{"derivedFrom":makeQuery(id+"F26.opExtrude","SWEPT_FACE",FACE,{"disambiguationData":[OSD([sQuery(id+"F25.wireOp",EDGE,"E146.right")])]})});
            var sketch = newSketch(context, id + "F29", { "sketchPlane" : qUnion([Q0])});
            skLineSegment(sketch, "E187.0.0", {"start": v(82, -22.16) * mm, "end": v(82, -29.16) * mm});
            skLineSegment(sketch, "E187.0.1", {"start": v(82, -29.16) * mm, "end": v(87, -29.16) * mm});
            skLineSegment(sketch, "E187.0.2", {"start": v(87, -29.16) * mm, "end": v(87, -22.16) * mm});
            skLineSegment(sketch, "E187.0.3", {"start": v(87, -22.16) * mm, "end": v(82, -22.16) * mm});
            skLineSegment(sketch, "E188.0.0", {"start": v(74, -22.16) * mm, "end": v(82, -22.16) * mm});
            skLineSegment(sketch, "E188.0.1", {"start": v(82, -22.16) * mm, "end": v(82, -17.16) * mm});
            skLineSegment(sketch, "E188.0.2", {"start": v(82, -17.16) * mm, "end": v(74, -17.16) * mm});
            skLineSegment(sketch, "E188.0.3", {"start": v(74, -17.16) * mm, "end": v(74, -22.16) * mm});
            skLineSegment(sketch, "E189.0", {"start": v(61.5, -17.16) * mm, "end": v(63.5, -17.16) * mm, "construction": true});
            skLineSegment(sketch, "E190", {"start": v(74, -22.16) * mm, "end": v(67.5, -22.16) * mm});
            skLineSegment(sketch, "E191.0.0", {"start": v(82, -39.16) * mm, "end": v(82, -46.16) * mm});
            skLineSegment(sketch, "E191.0.1", {"start": v(82, -46.16) * mm, "end": v(87, -46.16) * mm});
            skLineSegment(sketch, "E191.0.2", {"start": v(87, -46.16) * mm, "end": v(87, -39.16) * mm});
            skLineSegment(sketch, "E191.0.3", {"start": v(87, -39.16) * mm, "end": v(82, -39.16) * mm});
            skLineSegment(sketch, "E192", {"start": v(67.5, -22.16) * mm, "end": v(67.5, -27.86) * mm});
            skLineSegment(sketch, "E193", {"start": v(67.83, -30.42) * mm, "end": v(70.03, -38.72) * mm});
            skLineSegment(sketch, "E194", {"start": v(79.7, -46.16) * mm, "end": v(82, -46.16) * mm});
            skLineSegment(sketch, "E195", {"start": v(82, -29.16) * mm, "end": v(82, -39.16) * mm});
            skPoint(sketch, "E196.visualSharp", {"position": v(72, -46.16) * mm});
            skArc(sketch, "E196.filletArc", {"start": v(70.03, -38.72) * mm, "mid": v(73.6, -44.09) * mm, "end": v(79.7, -46.16) * mm});
            skPoint(sketch, "E197.visualSharp", {"position": v(67.5, -29.16) * mm});
            skArc(sketch, "E197.filletArc", {"start": v(67.5, -27.86) * mm, "mid": v(67.58, -29.15) * mm, "end": v(67.83, -30.42) * mm});
            skSolve(sketch);
        }
        {
            var Q0;
            Q0=qSketchRegion(id+"F29",true);
            extrude(context, id + "F30", {"entities" : qUnion([Q0]), "depth" : 5 * mm});
        }
    });
